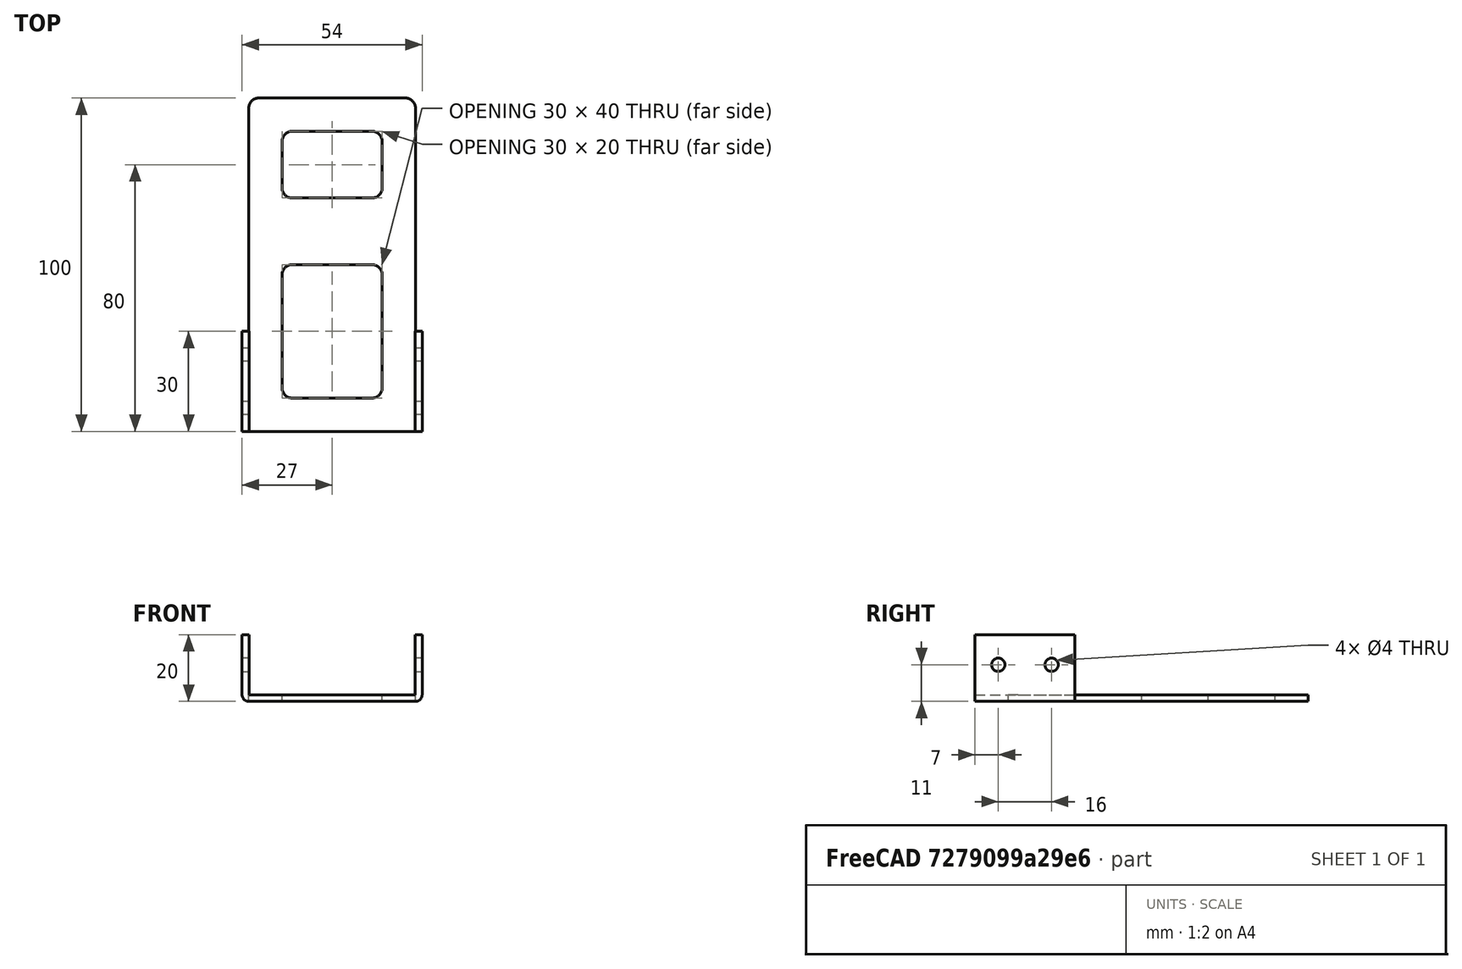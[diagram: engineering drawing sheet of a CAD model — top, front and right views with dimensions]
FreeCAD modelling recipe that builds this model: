
FCSTD DOCUMENT  (FreeCAD 0.21R33694 (Git))
Label: OJT1_T012_PEÇA
License: All rights reserved
LicenseURL: https://en.wikipedia.org/wiki/All_rights_reserved
objects: Part::Box×5, Part::Fillet×5, Part::Cut×5, Part::Cylinder×2, Part::MultiFuse×1, Part::Refine×1
note: 19 computed .brp shape members not serialized (recipe doc carries the construction recipe); baked Part::Feature solids carry a one-line shape summary decoded from their .brp

FEATURE [Part::Box] Box  label="Cub"
  AttacherType = Attacher::AttachEngine3D
  Height = 2
  Length = 50
  Width = 100
FEATURE [Part::Fillet] Fillet
  Base = -> Box
  Edges = 2 edges r=3: [Edge3,Edge7]
FEATURE [Part::Box] Box001  label="Cub001"
  AttacherType = Attacher::AttachEngine3D
  Height = 2
  Length = 30
  Placement = pos=(10,10,0) rot=(0,0,1;0rad)
  Width = 40
  expr: .Placement.Base.x = 10
  expr: .Placement.Base.y = 10
FEATURE [Part::Fillet] Fillet001
  Base = -> Box001
  Edges = 4 edges r=3: [Edge1,Edge3,Edge5,Edge7]
FEATURE [Part::Cut] Cut
  Base = -> Fillet
  Tool = -> Fillet001
FEATURE [Part::Box] Box002  label="Cub002"
  AttacherType = Attacher::AttachEngine3D
  Height = 2
  Length = 30
  Placement = pos=(10,70,0) rot=(0,0,1;0rad)
  Width = 20
  expr: .Placement.Base.x = 10
  expr: .Placement.Base.y = 70
FEATURE [Part::Fillet] Fillet002
  Base = -> Box002
  Edges = 4 edges r=3: [Edge1,Edge3,Edge5,Edge7]
FEATURE [Part::Cut] Cut001
  Base = -> Cut
  Tool = -> Fillet002
FEATURE [Part::Box] Box003  label="Cub003"
  AttacherType = Attacher::AttachEngine3D
  Height = 20
  Length = 54
  Width = 30
FEATURE [Part::Cylinder] Cylinder  label="Cilindre"
  Angle = 360
  AttacherType = Attacher::AttachEngine3D
  FirstAngle = 0
  Height = 54
  Placement = pos=(0,7,11) rot=(0,1,0;1.5708rad)
  Radius = 2
  SecondAngle = 0
  expr: .Placement.Base.y = 7
  expr: .Placement.Base.z = 11
  expr: .Placement.Rotation.Pitch = 90
FEATURE [Part::Cylinder] Cylinder001  label="Cilindre001"
  Angle = 360
  AttacherType = Attacher::AttachEngine3D
  FirstAngle = 0
  Height = 54
  Placement = pos=(0,23,11) rot=(0,1,0;1.5708rad)
  Radius = 2
  SecondAngle = 0
  expr: .Placement.Base.y = 23
  expr: .Placement.Base.z = 11
  expr: .Placement.Rotation.Pitch = 90
FEATURE [Part::Cut] Cut002
  Base = -> Box003
  Tool = -> Cylinder
FEATURE [Part::Cut] Cut003
  Base = -> Cut002
  Tool = -> Cylinder001
FEATURE [Part::Box] Box004  label="Cub004"
  AttacherType = Attacher::AttachEngine3D
  Height = 20
  Length = 49.8
  Placement = pos=(2.1,0,0) rot=(0,0,1;0rad)
  Width = 30
  expr: .Placement.Base.x = 2.1
FEATURE [Part::Cut] Cut004
  Base = -> Cut003
  Tool = -> Box004
FEATURE [Part::Fillet] Fillet003
  Base = -> Cut004
  Edges = 1 edges r=2: [Edge24]
FEATURE [Part::Fillet] Fillet004
  Base = -> Fillet003
  Edges = 1 edges r=2: [Edge23]
  Placement = pos=(-2,0,0) rot=(0,0,1;0rad)
FEATURE [Part::MultiFuse] Fusion
  Shapes = -> [Cut001,Fillet004]
FEATURE [Part::Refine] Fusion001
  Source = -> Fusion
